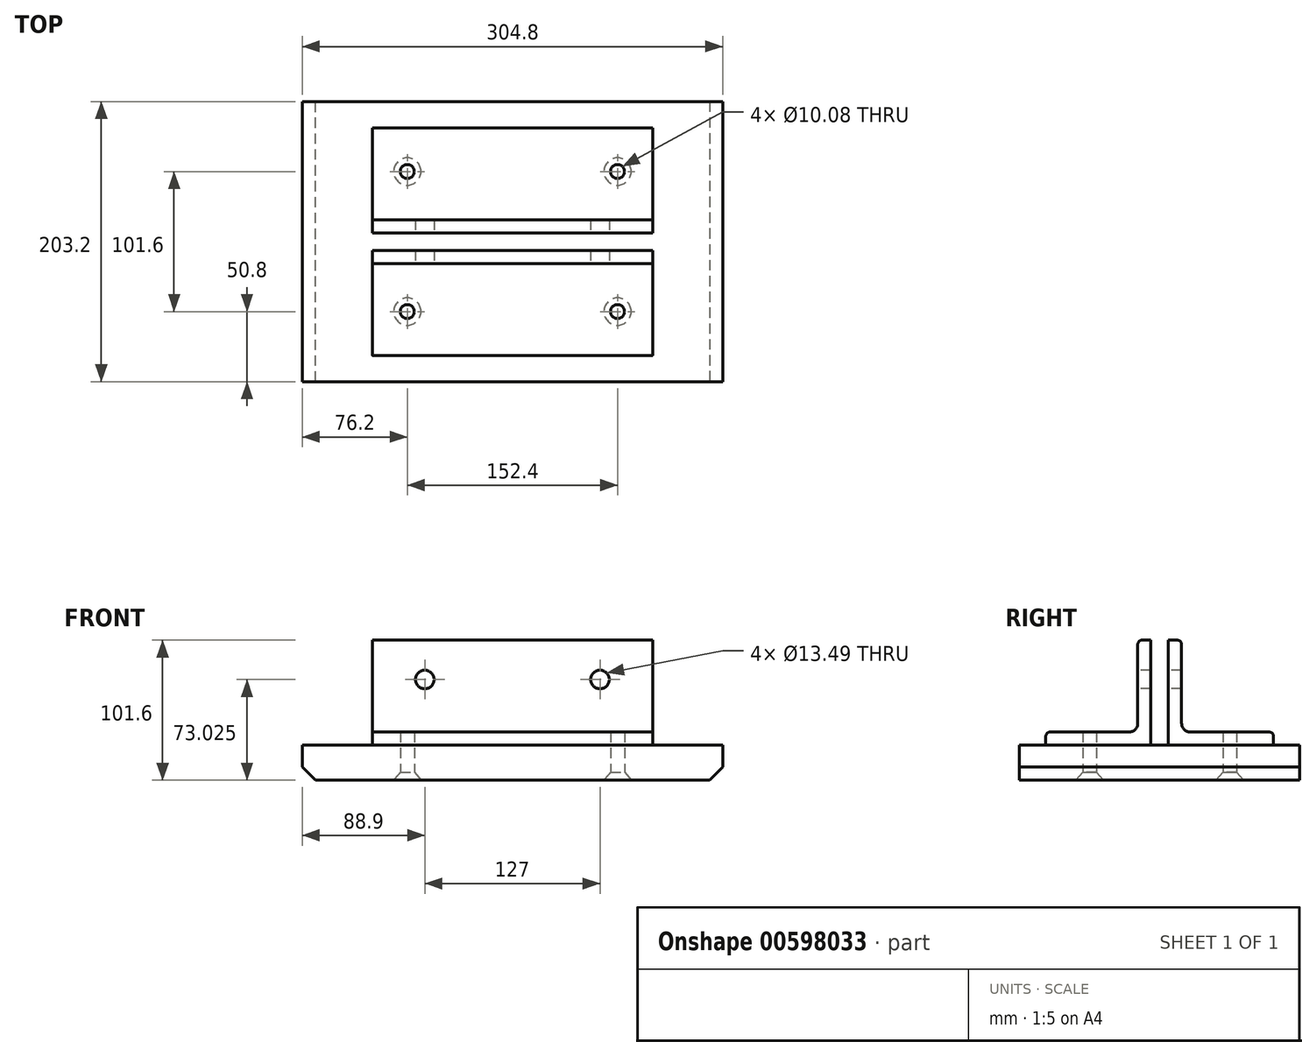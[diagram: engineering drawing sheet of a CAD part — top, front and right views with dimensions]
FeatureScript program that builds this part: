
annotation { "Feature Type Name" : "Feature", "Feature Type Description" : "" }
export const myFeature = defineFeature(function(context is Context, id is Id, definition is map)
    precondition{}
    {
        {
            var Q0;
            Q0=qCreatedBy(makeId("Front.planeOp"),FACE);
            var sketch = newSketch(context, id + "F0", { "sketchPlane" : qUnion([Q0])});
            skLineSegment(sketch, "E0.bottom", {"start": v(152.4, -12.7) * mm, "end": v(-152.4, -12.7) * mm});
            skLineSegment(sketch, "E0.top", {"start": v(152.4, 12.7) * mm, "end": v(-152.4, 12.7) * mm});
            skLineSegment(sketch, "E0.left", {"start": v(152.4, -12.7) * mm, "end": v(152.4, 12.7) * mm});
            skLineSegment(sketch, "E0.right", {"start": v(-152.4, -12.7) * mm, "end": v(-152.4, 12.7) * mm});
            skPoint(sketch, "E0.middle", {"position": v(0, 0) * mm});
            skSolve(sketch);
        }
        {
            var Q0;
            Q0 = qSketchRegion(id + "F0", true);
            extrude(context, id + "F1", {"entities" : qUnion([Q0]), "endBound" : BoundingType.SYMMETRIC, "depth" : 203.2 * mm, "offsetDistance" : 25.4 * mm});
        }
        {
            var Q0;
            Q0=qCreatedBy(makeId("Right.planeOp"),FACE);
            var sketch = newSketch(context, id + "F2", { "sketchPlane" : qUnion([Q0])});
            skLineSegment(sketch, "E1.0", {"start": v(-101.6, 12.7) * mm, "end": v(101.6, 12.7) * mm});
            skLineSegment(sketch, "E2", {"start": v(-82.55, 12.7) * mm, "end": v(-6.35, 12.7) * mm});
            skLineSegment(sketch, "E3", {"start": v(-6.35, 12.7) * mm, "end": v(-6.35, 88.9) * mm});
            skLineSegment(sketch, "E4", {"start": v(-6.35, 88.9) * mm, "end": v(-12.7, 88.9) * mm});
            skLineSegment(sketch, "E5", {"start": v(-15.88, 85.73) * mm, "end": v(-15.88, 28.58) * mm});
            skLineSegment(sketch, "E6", {"start": v(-22.23, 22.23) * mm, "end": v(-79.38, 22.23) * mm});
            skLineSegment(sketch, "E7", {"start": v(-82.55, 19.05) * mm, "end": v(-82.55, 12.7) * mm});
            skLineSegment(sketch, "E8.MirrorCS", {"start": v(82.55, 19.05) * mm, "end": v(82.55, 12.7) * mm});
            skLineSegment(sketch, "E9.MirrorCS", {"start": v(6.35, 88.9) * mm, "end": v(12.7, 88.9) * mm});
            skLineSegment(sketch, "E10.MirrorCS", {"start": v(22.23, 22.23) * mm, "end": v(79.38, 22.23) * mm});
            skLineSegment(sketch, "E11.MirrorCS", {"start": v(6.35, 12.7) * mm, "end": v(6.35, 88.9) * mm});
            skLineSegment(sketch, "E12.MirrorCS", {"start": v(15.88, 85.73) * mm, "end": v(15.88, 28.58) * mm});
            skLineSegment(sketch, "E13.MirrorCS", {"start": v(82.55, 12.7) * mm, "end": v(6.35, 12.7) * mm});
            skPoint(sketch, "E14.visualSharp", {"position": v(-82.55, 22.23) * mm});
            skArc(sketch, "E14.filletArc", {"start": v(-79.38, 22.23) * mm, "mid": v(-81.62, 21.3) * mm, "end": v(-82.55, 19.05) * mm});
            skPoint(sketch, "E15.visualSharp", {"position": v(-15.88, 88.9) * mm});
            skArc(sketch, "E15.filletArc", {"start": v(-12.7, 88.9) * mm, "mid": v(-14.95, 87.97) * mm, "end": v(-15.88, 85.73) * mm});
            skPoint(sketch, "E16.visualSharp", {"position": v(15.88, 88.9) * mm});
            skArc(sketch, "E16.filletArc", {"start": v(15.88, 85.73) * mm, "mid": v(14.95, 87.97) * mm, "end": v(12.7, 88.9) * mm});
            skPoint(sketch, "E17.visualSharp", {"position": v(82.55, 22.23) * mm});
            skArc(sketch, "E17.filletArc", {"start": v(82.55, 19.05) * mm, "mid": v(81.62, 21.3) * mm, "end": v(79.38, 22.23) * mm});
            skPoint(sketch, "E18.visualSharp", {"position": v(-15.88, 22.23) * mm});
            skArc(sketch, "E18.filletArc", {"start": v(-22.23, 22.23) * mm, "mid": v(-17.73, 24.08) * mm, "end": v(-15.88, 28.58) * mm});
            skPoint(sketch, "E19.visualSharp", {"position": v(15.88, 22.23) * mm});
            skArc(sketch, "E19.filletArc", {"start": v(15.88, 28.58) * mm, "mid": v(17.73, 24.08) * mm, "end": v(22.23, 22.23) * mm});
            skSolve(sketch);
        }
        {
            var Q0;
            Q0 = qSketchRegion(id + "F2", true);
            extrude(context, id + "F3", {"entities" : qUnion([Q0]), "operationType" : NewBodyOperationType.ADD, "endBound" : BoundingType.SYMMETRIC, "depth" : 203.2 * mm, "offsetDistance" : 25.4 * mm});
        }
        {
            var Q0;
            Q0=makeQuery(id+"F1.opExtrude","SWEPT_FACE",FACE,{"disambiguationData":[OSD([sQuery(id+"F0.wireOp",EDGE,"E0.bottom")])]});
            var sketch = newSketch(context, id + "F4", { "sketchPlane" : qUnion([Q0])});
            skLineSegment(sketch, "E20", {"start": v(-76.2, 140.36) * mm, "end": v(-76.2, -170.48) * mm, "construction": true});
            skLineSegment(sketch, "E21", {"start": v(-199.52, 50.8) * mm, "end": v(223.93, 50.8) * mm, "construction": true});
            skLineSegment(sketch, "E22.MirrorCS", {"start": v(-199.52, -50.8) * mm, "end": v(223.93, -50.8) * mm, "construction": true});
            skLineSegment(sketch, "E23.MirrorCS", {"start": v(76.2, 140.36) * mm, "end": v(76.2, -170.48) * mm, "construction": true});
            skPoint(sketch, "E24", {"position": v(-76.2, 50.8) * mm});
            skPoint(sketch, "E25", {"position": v(76.2, 50.8) * mm});
            skPoint(sketch, "E26", {"position": v(76.2, -50.8) * mm});
            skPoint(sketch, "E27", {"position": v(-76.2, -50.8) * mm});
            skSolve(sketch);
        }
        {
            var Q0;
            Q0=sQuery(id+"F4.wireOp",VERTEX,"E24");
            var Q1;
            Q1=sQuery(id+"F4.wireOp",VERTEX,"E25");
            var Q2;
            Q2=sQuery(id+"F4.wireOp",VERTEX,"E26");
            var Q3;
            Q3=sQuery(id+"F4.wireOp",VERTEX,"E27");
            var Q4;
            Q4=makeQuery(id+"F1.opExtrude","SWEPT_BODY",BODY,{"disambiguationData":[OSD([sQuery(id+"F0.wireOp",EDGE,"E0.bottom"),sQuery(id+"F0.wireOp",EDGE,"E0.top"),sQuery(id+"F0.wireOp",EDGE,"E0.left"),sQuery(id+"F0.wireOp",EDGE,"E0.right")])]});
            hole(context, id + "F5", {"style" : HoleStyle.C_SINK, "endStyle" : HoleEndStyle.THROUGH, "standardTappedOrClearance" : lookupTablePath({ "standard" : "ANSI", "fit" : "Normal (ASME)", "size" : "3/8", "type" : "Clearance" }), "standardBlindInLast" : lookupTablePath({ "fit" : "Free", "standard" : "ANSI", "size" : "3/8", "type" : "Clearance" }), "holeDiameter" : 10.08 * mm, "cSinkDiameter" : 19.84 * mm, "cSinkAngle" : 82 * degree, "majorDiameter" : 6.35 * mm, "isTappedThrough" : true, "tappedDepth" : 12.7 * mm, "tapClearance" : 3, "startFromSketch" : true, "locations" : qUnion([Q0, Q1, Q2, Q3]), "scope" : qUnion([Q4])});
        }
        {
            var Q0;
            Q0=makeQuery(id+"F3.opExtrude","SWEPT_FACE",FACE,{"disambiguationData":[OSD([sQuery(id+"F2.wireOp",EDGE,"E5")])]});
            var sketch = newSketch(context, id + "F6", { "sketchPlane" : qUnion([Q0])});
            skPoint(sketch, "E28", {"position": v(-63.5, 60.33) * mm});
            skPoint(sketch, "E29", {"position": v(63.5, 60.33) * mm});
            skSolve(sketch);
        }
        {
            var Q0;
            Q0=sQuery(id+"F6.wireOp",VERTEX,"E28");
            var Q1;
            Q1=sQuery(id+"F6.wireOp",VERTEX,"E29");
            var Q2;
            Q2=makeQuery(id+"F1.opExtrude","SWEPT_BODY",BODY,{"disambiguationData":[OSD([sQuery(id+"F0.wireOp",EDGE,"E0.bottom"),sQuery(id+"F0.wireOp",EDGE,"E0.top"),sQuery(id+"F0.wireOp",EDGE,"E0.left"),sQuery(id+"F0.wireOp",EDGE,"E0.right")])]});
            hole(context, id + "F7", {"style" : HoleStyle.SIMPLE, "endStyle" : HoleEndStyle.THROUGH, "standardTappedOrClearance" : lookupTablePath({ "standard" : "ANSI", "fit" : "Normal (ASME)", "size" : "1/2", "type" : "Clearance" }), "standardBlindInLast" : lookupTablePath({ "fit" : "Free", "standard" : "ANSI", "size" : "1/2", "type" : "Clearance" }), "holeDiameter" : 13.5 * mm, "majorDiameter" : 6.35 * mm, "isTappedThrough" : true, "tappedDepth" : 12.7 * mm, "tapClearance" : 3, "startFromSketch" : true, "locations" : qUnion([Q0, Q1]), "scope" : qUnion([Q2])});
        }
        {
            var Q0;
            Q0=makeQuery(id+"F1.opExtrude","SWEPT_EDGE",EDGE,{"disambiguationData":[OSD([sQuery(id+"F0.wireOp",EDGE,"E0.bottom"),sQuery(id+"F0.wireOp",EDGE,"E0.left")])]});
            chamfer(context, id + "F8", {"entities" : qUnion([Q0]), "width" : 9.52 * mm, "tangentPropagation" : true});
        }
        {
            var Q0;
            Q0=makeQuery(id+"F1.opExtrude","SWEPT_EDGE",EDGE,{"disambiguationData":[OSD([sQuery(id+"F0.wireOp",EDGE,"E0.bottom"),sQuery(id+"F0.wireOp",EDGE,"E0.right")])]});
            chamfer(context, id + "F9", {"entities" : qUnion([Q0]), "width" : 9.52 * mm, "tangentPropagation" : true});
        }
    });
